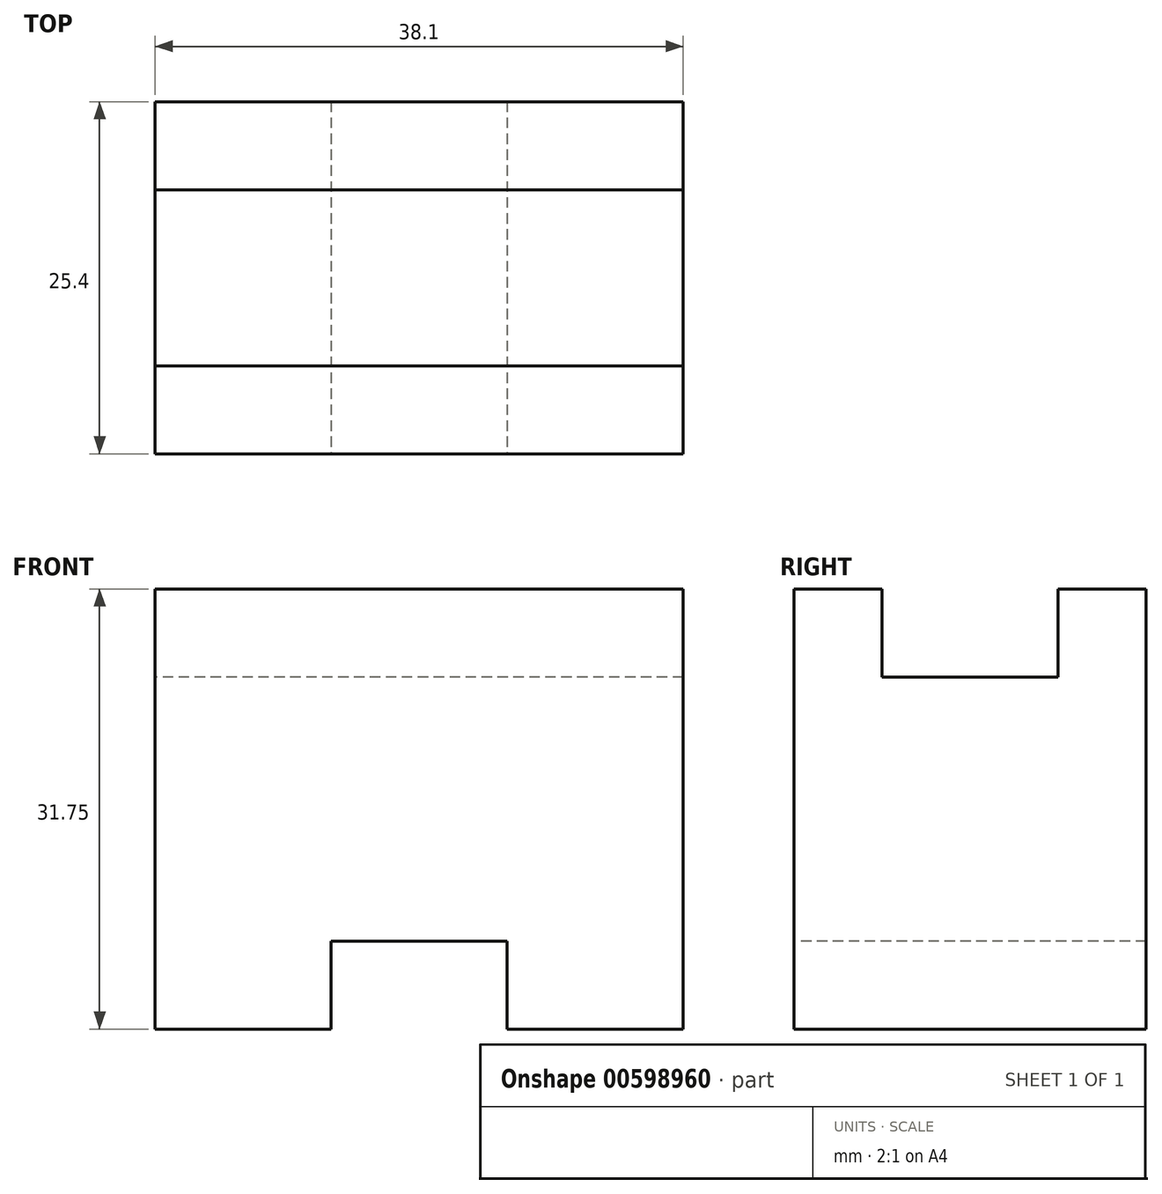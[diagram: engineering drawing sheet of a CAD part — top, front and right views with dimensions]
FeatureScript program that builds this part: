
annotation { "Feature Type Name" : "Feature", "Feature Type Description" : "" }
export const myFeature = defineFeature(function(context is Context, id is Id, definition is map)
    precondition{}
    {
        {
            var Q0;
            Q0=qCreatedBy(makeId("Right.planeOp"),FACE);
            var sketch = newSketch(context, id + "F0", { "sketchPlane" : qUnion([Q0])});
            skLineSegment(sketch, "E0", {"start": v(0, 0) * mm, "end": v(0, 31.75) * mm});
            skLineSegment(sketch, "E1", {"start": v(0, 31.75) * mm, "end": v(6.35, 31.75) * mm});
            skLineSegment(sketch, "E2", {"start": v(6.35, 31.75) * mm, "end": v(6.35, 25.4) * mm});
            skLineSegment(sketch, "E3", {"start": v(6.35, 25.4) * mm, "end": v(19.05, 25.4) * mm});
            skLineSegment(sketch, "E4", {"start": v(19.05, 25.4) * mm, "end": v(19.05, 31.75) * mm});
            skLineSegment(sketch, "E5", {"start": v(19.05, 31.75) * mm, "end": v(25.4, 31.75) * mm});
            skLineSegment(sketch, "E6", {"start": v(25.4, 31.75) * mm, "end": v(25.4, 0) * mm});
            skLineSegment(sketch, "E7", {"start": v(25.4, 0) * mm, "end": v(0, 0) * mm});
            skSolve(sketch);
        }
        {
            var Q0;
            Q0 = qSketchRegion(id + "F0", true);
            extrude(context, id + "F1", {"entities" : qUnion([Q0]), "depth" : 25.4 * mm, "offsetDistance" : 25.4 * mm});
        }
        {
            var Q0;
            Q0 = qSketchRegion(id + "F0", true);
            extrude(context, id + "F2", {"entities" : qUnion([Q0]), "operationType" : NewBodyOperationType.ADD, "depth" : 38.1 * mm, "offsetDistance" : 25.4 * mm});
        }
        {
            var Q0;
            {var subQ0=sQuery(id+"F0.wireOp",EDGE,"E0");Q0=makeQuery(id+"F2.boolean.opBoolean","MERGE",FACE,{"derivedFrom":[makeQuery(id+"F1.opExtrude","SWEPT_FACE",FACE,{"disambiguationData":[OSD([subQ0])]}),makeQuery(id+"F2.opExtrude","SWEPT_FACE",FACE,{"disambiguationData":[OSD([subQ0])]})]});}
            var sketch = newSketch(context, id + "F3", { "sketchPlane" : qUnion([Q0])});
            skLineSegment(sketch, "E8", {"start": v(0, 0) * mm, "end": v(12.7, 0) * mm});
            skLineSegment(sketch, "E9", {"start": v(12.7, 0) * mm, "end": v(12.7, 6.35) * mm});
            skLineSegment(sketch, "E10", {"start": v(12.7, 6.35) * mm, "end": v(25.4, 6.35) * mm});
            skLineSegment(sketch, "E11", {"start": v(25.4, 6.35) * mm, "end": v(25.4, 0) * mm});
            skLineSegment(sketch, "E12", {"start": v(25.4, 0) * mm, "end": v(38.1, 0) * mm});
            skLineSegment(sketch, "E13", {"start": v(38.1, 0) * mm, "end": v(38.1, 31.75) * mm});
            skLineSegment(sketch, "E14", {"start": v(38.1, 31.75) * mm, "end": v(0, 31.75) * mm});
            skLineSegment(sketch, "E15", {"start": v(0, 31.75) * mm, "end": v(0, 0) * mm});
            skSolve(sketch);
        }
        {
            var Q0;
            {var subQ0=sQuery(id+"F3.wireOp",EDGE,"E9");Q0=makeQuery(id+"F3.imprint","IMPRINT",FACE,{"disambiguationData":[TD([[makeQuery(id+"F3.imprint","IMPRINT",EDGE,{"derivedFrom":subQ0}),-1.0]])]});}
            extrude(context, id + "F4", {"entities" : qUnion([Q0]), "operationType" : NewBodyOperationType.REMOVE, "oppositeDirection" : true, "depth" : 25.4 * mm, "offsetDistance" : 25.4 * mm});
        }
    });
